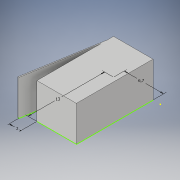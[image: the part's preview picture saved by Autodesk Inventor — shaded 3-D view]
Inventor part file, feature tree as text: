
AUTODESK INVENTOR PART (.ipt)
format: ipt  version: 2019 (Build 230136000, 136)  size: 101,888 bytes
history: native  units: mm
features: extrude x2, sketch x1
ambient origin geometry x8: Origin, YZ Plane, XZ Plane, XY Plane, X Axis, Y Axis, Z Axis, Center Point
bodies: Solid1 (feature_tree)
feature tree (3):
  sketch  "Sketch1"  dims[d0=13.0mm d1=6.7mm d2=2.0mm d3=6.0mm d4=0.0mm d5=6.0mm d6=0.0mm]
  extrude  "Extrusion1"  Depth=6.7mm
  extrude  "Extrusion2"  Depth=6.0mm
